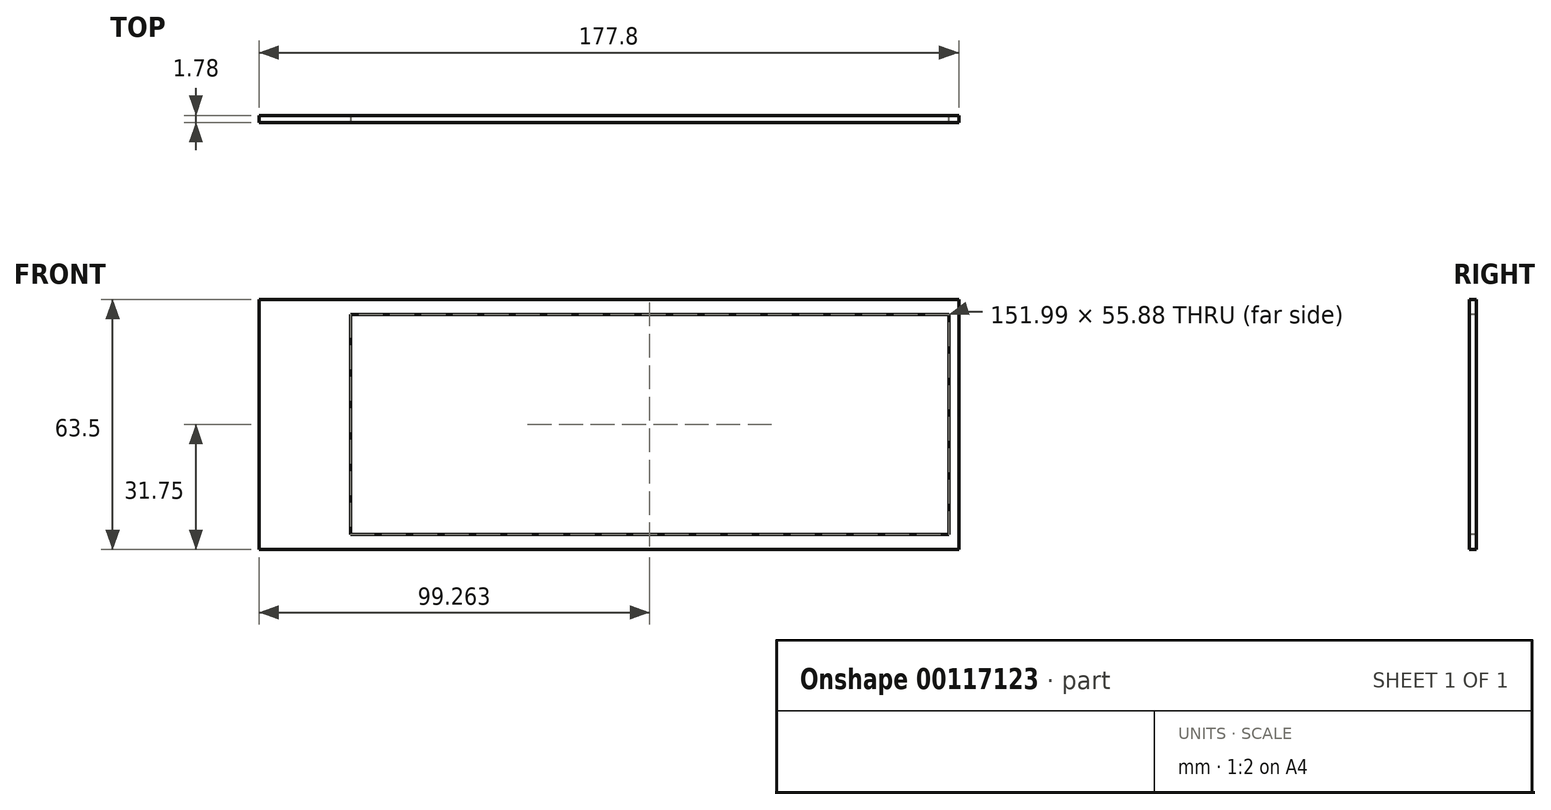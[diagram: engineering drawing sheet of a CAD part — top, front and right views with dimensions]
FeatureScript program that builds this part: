
annotation { "Feature Type Name" : "Feature", "Feature Type Description" : "" }
export const myFeature = defineFeature(function(context is Context, id is Id, definition is map)
    precondition{}
    {
        {
            var Q0;
            Q0=qCreatedBy(makeId("Front.planeOp"),FACE);
            var sketch = newSketch(context, id + "F0", { "sketchPlane" : qUnion([Q0])});
            skLineSegment(sketch, "E0.bottom", {"start": v(88.9, -31.75) * mm, "end": v(-88.9, -31.75) * mm});
            skLineSegment(sketch, "E0.top", {"start": v(88.9, 31.75) * mm, "end": v(-88.9, 31.75) * mm});
            skLineSegment(sketch, "E0.left", {"start": v(88.9, -31.75) * mm, "end": v(88.9, 31.75) * mm});
            skLineSegment(sketch, "E0.right", {"start": v(-88.9, -31.75) * mm, "end": v(-88.9, 31.75) * mm});
            skPoint(sketch, "E0.middle", {"position": v(0, 0) * mm});
            skLineSegment(sketch, "E1.bottom", {"start": v(86.36, -27.94) * mm, "end": v(-86.36, -27.94) * mm});
            skLineSegment(sketch, "E1.top", {"start": v(86.36, 27.94) * mm, "end": v(-86.36, 27.94) * mm});
            skLineSegment(sketch, "E1.left", {"start": v(86.36, -27.94) * mm, "end": v(86.36, 27.94) * mm});
            skLineSegment(sketch, "E1.right", {"start": v(-86.36, -27.94) * mm, "end": v(-86.36, 27.94) * mm});
            skLineSegment(sketch, "E2.bottom", {"start": v(-79.45, 27.94) * mm, "end": v(-72.54, 27.94) * mm});
            skLineSegment(sketch, "E2.top", {"start": v(-79.45, -27.94) * mm, "end": v(-72.54, -27.94) * mm});
            skLineSegment(sketch, "E2.left", {"start": v(-79.45, 27.94) * mm, "end": v(-79.45, -27.94) * mm});
            skLineSegment(sketch, "E2.right", {"start": v(-72.54, 27.94) * mm, "end": v(-72.54, -27.94) * mm});
            skLineSegment(sketch, "E3.1.0.0", {"start": v(-65.63, 27.94) * mm, "end": v(-58.72, 27.94) * mm});
            skLineSegment(sketch, "E3.1.0.1", {"start": v(-65.63, -27.94) * mm, "end": v(-58.72, -27.94) * mm});
            skLineSegment(sketch, "E3.1.0.2", {"start": v(-65.63, 27.94) * mm, "end": v(-65.63, -27.94) * mm});
            skLineSegment(sketch, "E3.1.0.3", {"start": v(-58.72, 27.94) * mm, "end": v(-58.72, -27.94) * mm});
            skLineSegment(sketch, "E3.2.0.0", {"start": v(-51.82, 27.94) * mm, "end": v(-44.9, 27.94) * mm});
            skLineSegment(sketch, "E3.2.0.1", {"start": v(-51.82, -27.94) * mm, "end": v(-44.9, -27.94) * mm});
            skLineSegment(sketch, "E3.2.0.2", {"start": v(-51.82, 27.94) * mm, "end": v(-51.82, -27.94) * mm});
            skLineSegment(sketch, "E3.2.0.3", {"start": v(-44.9, 27.94) * mm, "end": v(-44.9, -27.94) * mm});
            skLineSegment(sketch, "E3.direction1", {"start": v(-79.45, -27.94) * mm, "end": v(-65.63, -27.94) * mm, "construction": true});
            skLineSegment(sketch, "E4.0.3.0", {"start": v(-38, 27.94) * mm, "end": v(-31.09, 27.94) * mm});
            skLineSegment(sketch, "E4.3.3.0", {"start": v(-38, -27.94) * mm, "end": v(-31.09, -27.94) * mm});
            skLineSegment(sketch, "E4.6.3.0", {"start": v(-38, 27.94) * mm, "end": v(-38, -27.94) * mm});
            skLineSegment(sketch, "E4.9.3.0", {"start": v(-31.09, 27.94) * mm, "end": v(-31.09, -27.94) * mm});
            skLineSegment(sketch, "E4.0.4.0", {"start": v(-24.18, 27.94) * mm, "end": v(-17.27, 27.94) * mm});
            skLineSegment(sketch, "E4.3.4.0", {"start": v(-24.18, -27.94) * mm, "end": v(-17.27, -27.94) * mm});
            skLineSegment(sketch, "E4.6.4.0", {"start": v(-24.18, 27.94) * mm, "end": v(-24.18, -27.94) * mm});
            skLineSegment(sketch, "E4.9.4.0", {"start": v(-17.27, 27.94) * mm, "end": v(-17.27, -27.94) * mm});
            skLineSegment(sketch, "E4.0.5.0", {"start": v(-10.36, 27.94) * mm, "end": v(-3.45, 27.94) * mm});
            skLineSegment(sketch, "E4.3.5.0", {"start": v(-10.36, -27.94) * mm, "end": v(-3.45, -27.94) * mm});
            skLineSegment(sketch, "E4.6.5.0", {"start": v(-10.36, 27.94) * mm, "end": v(-10.36, -27.94) * mm});
            skLineSegment(sketch, "E4.9.5.0", {"start": v(-3.45, 27.94) * mm, "end": v(-3.45, -27.94) * mm});
            skLineSegment(sketch, "E4.0.6.0", {"start": v(3.45, 27.94) * mm, "end": v(10.36, 27.94) * mm});
            skLineSegment(sketch, "E4.3.6.0", {"start": v(3.45, -27.94) * mm, "end": v(10.36, -27.94) * mm});
            skLineSegment(sketch, "E4.6.6.0", {"start": v(3.45, 27.94) * mm, "end": v(3.45, -27.94) * mm});
            skLineSegment(sketch, "E4.9.6.0", {"start": v(10.36, 27.94) * mm, "end": v(10.36, -27.94) * mm});
            skLineSegment(sketch, "E4.0.7.0", {"start": v(17.27, 27.94) * mm, "end": v(24.18, 27.94) * mm});
            skLineSegment(sketch, "E4.3.7.0", {"start": v(17.27, -27.94) * mm, "end": v(24.18, -27.94) * mm});
            skLineSegment(sketch, "E4.6.7.0", {"start": v(17.27, 27.94) * mm, "end": v(17.27, -27.94) * mm});
            skLineSegment(sketch, "E4.9.7.0", {"start": v(24.18, 27.94) * mm, "end": v(24.18, -27.94) * mm});
            skLineSegment(sketch, "E4.0.8.0", {"start": v(31.09, 27.94) * mm, "end": v(38, 27.94) * mm});
            skLineSegment(sketch, "E4.3.8.0", {"start": v(31.09, -27.94) * mm, "end": v(38, -27.94) * mm});
            skLineSegment(sketch, "E4.6.8.0", {"start": v(31.09, 27.94) * mm, "end": v(31.09, -27.94) * mm});
            skLineSegment(sketch, "E4.9.8.0", {"start": v(38, 27.94) * mm, "end": v(38, -27.94) * mm});
            skLineSegment(sketch, "E4.0.9.0", {"start": v(44.9, 27.94) * mm, "end": v(51.82, 27.94) * mm});
            skLineSegment(sketch, "E4.3.9.0", {"start": v(44.9, -27.94) * mm, "end": v(51.82, -27.94) * mm});
            skLineSegment(sketch, "E4.6.9.0", {"start": v(44.9, 27.94) * mm, "end": v(44.9, -27.94) * mm});
            skLineSegment(sketch, "E4.9.9.0", {"start": v(51.82, 27.94) * mm, "end": v(51.82, -27.94) * mm});
            skLineSegment(sketch, "E4.0.10.0", {"start": v(58.72, 27.94) * mm, "end": v(65.63, 27.94) * mm});
            skLineSegment(sketch, "E4.3.10.0", {"start": v(58.72, -27.94) * mm, "end": v(65.63, -27.94) * mm});
            skLineSegment(sketch, "E4.6.10.0", {"start": v(58.72, 27.94) * mm, "end": v(58.72, -27.94) * mm});
            skLineSegment(sketch, "E4.9.10.0", {"start": v(65.63, 27.94) * mm, "end": v(65.63, -27.94) * mm});
            skLineSegment(sketch, "E4.0.11.0", {"start": v(72.54, 27.94) * mm, "end": v(79.45, 27.94) * mm});
            skLineSegment(sketch, "E4.3.11.0", {"start": v(72.54, -27.94) * mm, "end": v(79.45, -27.94) * mm});
            skLineSegment(sketch, "E4.6.11.0", {"start": v(72.54, 27.94) * mm, "end": v(72.54, -27.94) * mm});
            skLineSegment(sketch, "E4.9.11.0", {"start": v(79.45, 27.94) * mm, "end": v(79.45, -27.94) * mm});
            skSolve(sketch);
        }
        {
            var Q0;
            Q0 = qSketchRegion(id + "F0", true);
            var Q1;
            Q1=makeQuery(id+"F0.imprint","IMPRINT",FACE,{"disambiguationData":[TD([[makeQuery(id+"F0.imprint","IMPRINT",EDGE,{"derivedFrom":sQuery(id+"F0.wireOp",EDGE,"E2.bottom")}),-1.0]])]});
            var Q2;
            Q2=makeQuery(id+"F0.imprint","IMPRINT",FACE,{"disambiguationData":[TD([[makeQuery(id+"F0.imprint","IMPRINT",EDGE,{"derivedFrom":sQuery(id+"F0.wireOp",EDGE,"E3.1.0.0")}),-1.0]])]});
            var Q3;
            Q3=makeQuery(id+"F0.imprint","IMPRINT",FACE,{"disambiguationData":[TD([[makeQuery(id+"F0.imprint","IMPRINT",EDGE,{"derivedFrom":sQuery(id+"F0.wireOp",EDGE,"E3.2.0.0")}),-1.0]])]});
            var Q4;
            Q4=makeQuery(id+"F0.imprint","IMPRINT",FACE,{"disambiguationData":[TD([[makeQuery(id+"F0.imprint","IMPRINT",EDGE,{"derivedFrom":sQuery(id+"F0.wireOp",EDGE,"E4.0.3.0")}),-1.0]])]});
            var Q5;
            Q5=makeQuery(id+"F0.imprint","IMPRINT",FACE,{"disambiguationData":[TD([[makeQuery(id+"F0.imprint","IMPRINT",EDGE,{"derivedFrom":sQuery(id+"F0.wireOp",EDGE,"E4.0.4.0")}),-1.0]])]});
            var Q6;
            Q6=makeQuery(id+"F0.imprint","IMPRINT",FACE,{"disambiguationData":[TD([[makeQuery(id+"F0.imprint","IMPRINT",EDGE,{"derivedFrom":sQuery(id+"F0.wireOp",EDGE,"E4.0.5.0")}),-1.0]])]});
            var Q7;
            Q7=makeQuery(id+"F0.imprint","IMPRINT",FACE,{"disambiguationData":[TD([[makeQuery(id+"F0.imprint","IMPRINT",EDGE,{"derivedFrom":sQuery(id+"F0.wireOp",EDGE,"E4.0.6.0")}),-1.0]])]});
            var Q8;
            Q8=makeQuery(id+"F0.imprint","IMPRINT",FACE,{"disambiguationData":[TD([[makeQuery(id+"F0.imprint","IMPRINT",EDGE,{"derivedFrom":sQuery(id+"F0.wireOp",EDGE,"E4.0.7.0")}),-1.0]])]});
            var Q9;
            Q9=makeQuery(id+"F0.imprint","IMPRINT",FACE,{"disambiguationData":[TD([[makeQuery(id+"F0.imprint","IMPRINT",EDGE,{"derivedFrom":sQuery(id+"F0.wireOp",EDGE,"E4.0.8.0")}),-1.0]])]});
            var Q10;
            Q10=makeQuery(id+"F0.imprint","IMPRINT",FACE,{"disambiguationData":[TD([[makeQuery(id+"F0.imprint","IMPRINT",EDGE,{"derivedFrom":sQuery(id+"F0.wireOp",EDGE,"E4.0.9.0")}),-1.0]])]});
            var Q11;
            Q11=makeQuery(id+"F0.imprint","IMPRINT",FACE,{"disambiguationData":[TD([[makeQuery(id+"F0.imprint","IMPRINT",EDGE,{"derivedFrom":sQuery(id+"F0.wireOp",EDGE,"E4.0.10.0")}),-1.0]])]});
            var Q12;
            Q12=makeQuery(id+"F0.imprint","IMPRINT",FACE,{"disambiguationData":[TD([[makeQuery(id+"F0.imprint","IMPRINT",EDGE,{"derivedFrom":sQuery(id+"F0.wireOp",EDGE,"E4.0.11.0")}),-1.0]])]});
            extrude(context, id + "F1", {"entities" : qUnion([Q0, Q1, Q2, Q3, Q4, Q5, Q6, Q7, Q8, Q9, Q10, Q11, Q12]), "depth" : 1.78 * mm});
        }
        {
            var Q0;
            Q0=makeQuery(id+"F1.opExtrude","CAP_FACE",FACE,{"disambiguationData":[OSD([sQuery(id+"F0.wireOp",EDGE,"E0.bottom"),sQuery(id+"F0.wireOp",EDGE,"E0.top"),sQuery(id+"F0.wireOp",EDGE,"E0.left"),sQuery(id+"F0.wireOp",EDGE,"E0.right"),sQuery(id+"F0.wireOp",EDGE,"E1.bottom"),sQuery(id+"F0.wireOp",EDGE,"E1.top"),sQuery(id+"F0.wireOp",EDGE,"E1.left"),sQuery(id+"F0.wireOp",EDGE,"E1.right"),sQuery(id+"F0.wireOp",EDGE,"E2.left"),sQuery(id+"F0.wireOp",EDGE,"E2.right"),sQuery(id+"F0.wireOp",EDGE,"E3.1.0.2"),sQuery(id+"F0.wireOp",EDGE,"E3.1.0.3"),sQuery(id+"F0.wireOp",EDGE,"E3.2.0.2"),sQuery(id+"F0.wireOp",EDGE,"E3.2.0.3"),sQuery(id+"F0.wireOp",EDGE,"E4.6.3.0"),sQuery(id+"F0.wireOp",EDGE,"E4.9.3.0"),sQuery(id+"F0.wireOp",EDGE,"E4.6.4.0"),sQuery(id+"F0.wireOp",EDGE,"E4.9.4.0"),sQuery(id+"F0.wireOp",EDGE,"E4.6.5.0"),sQuery(id+"F0.wireOp",EDGE,"E4.9.5.0"),sQuery(id+"F0.wireOp",EDGE,"E4.6.6.0"),sQuery(id+"F0.wireOp",EDGE,"E4.9.6.0"),sQuery(id+"F0.wireOp",EDGE,"E4.6.7.0"),sQuery(id+"F0.wireOp",EDGE,"E4.9.7.0"),sQuery(id+"F0.wireOp",EDGE,"E4.6.8.0"),sQuery(id+"F0.wireOp",EDGE,"E4.9.8.0"),sQuery(id+"F0.wireOp",EDGE,"E4.6.9.0"),sQuery(id+"F0.wireOp",EDGE,"E4.9.9.0"),sQuery(id+"F0.wireOp",EDGE,"E4.6.10.0"),sQuery(id+"F0.wireOp",EDGE,"E4.9.10.0"),sQuery(id+"F0.wireOp",EDGE,"E4.6.11.0"),sQuery(id+"F0.wireOp",EDGE,"E4.9.11.0")])],"isStart":false});
            var sketch = newSketch(context, id + "F2", { "sketchPlane" : qUnion([Q0])});
            skLineSegment(sketch, "E5.bottom", {"start": v(-86.36, 27.94) * mm, "end": v(-65.63, 27.94) * mm});
            skLineSegment(sketch, "E5.top", {"start": v(-86.36, -27.94) * mm, "end": v(-65.63, -27.94) * mm});
            skLineSegment(sketch, "E5.left", {"start": v(-86.36, 27.94) * mm, "end": v(-86.36, -27.94) * mm});
            skLineSegment(sketch, "E5.right", {"start": v(-65.63, 27.94) * mm, "end": v(-65.63, -27.94) * mm});
            skSolve(sketch);
        }
        {
            var Q0;
            Q0 = qSketchRegion(id + "F2", true);
            extrude(context, id + "F3", {"entities" : qUnion([Q0]), "operationType" : NewBodyOperationType.ADD, "oppositeDirection" : true, "depth" : 1.78 * mm});
        }
    });
